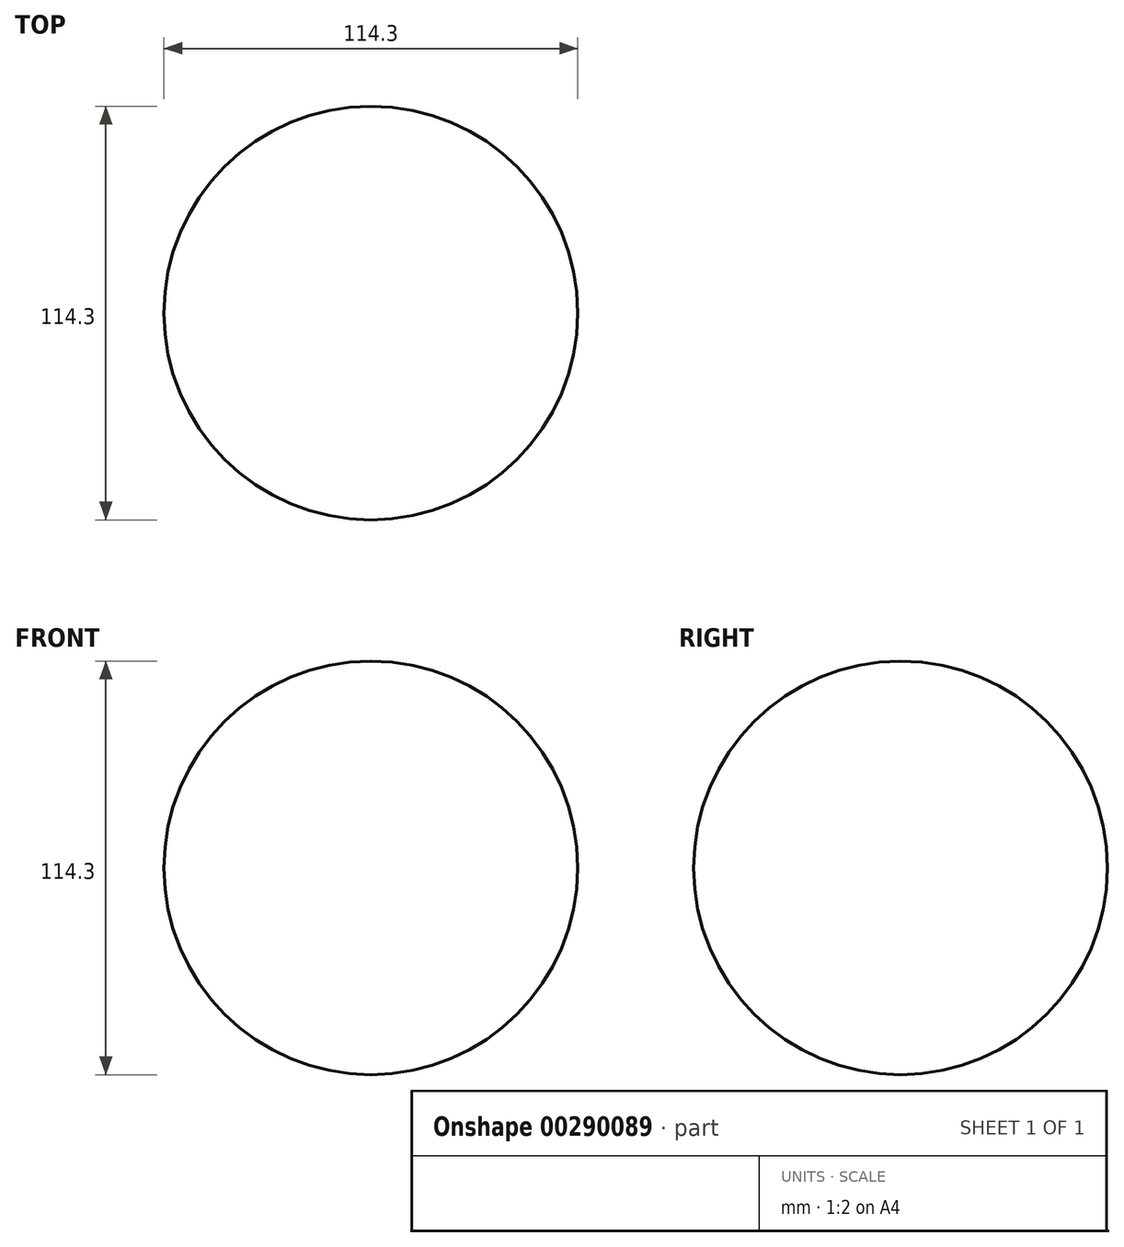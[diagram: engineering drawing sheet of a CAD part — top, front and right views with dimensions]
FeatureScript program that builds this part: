
annotation { "Feature Type Name" : "Feature", "Feature Type Description" : "" }
export const myFeature = defineFeature(function(context is Context, id is Id, definition is map)
    precondition{}
    {
        {
            var Q0;
            Q0=qCreatedBy(makeId("Top.planeOp"),FACE);
            var sketch = newSketch(context, id + "F0", { "sketchPlane" : qUnion([Q0])});
            skArc(sketch, "E0", {"start": v(0, 57.15) * mm, "mid": v(-57.15, 0) * mm, "end": v(0, -57.15) * mm});
            skLineSegment(sketch, "E1", {"start": v(0, 57.15) * mm, "end": v(0, -57.15) * mm});
            skSolve(sketch);
        }
        {
            var Q0;
            Q0=makeQuery(id+"F0.imprint","IMPRINT",FACE,{"disambiguationData":[TD([[makeQuery(id+"F0.imprint","IMPRINT",EDGE,{"derivedFrom":sQuery(id+"F0.wireOp",EDGE,"E0")}),1.0]])]});
            var Q1;
            Q1=sQuery(id+"F0.wireOp",EDGE,"E1");
            var Q2;
            Q2=sQuery(id+"F0.wireOp",EDGE,"E1");
            revolve(context, id + "F1", {"entities" : qUnion([Q0]), "surfaceEntities" : qUnion([Q1]), "axis" : qUnion([Q2]), "revolveType" : RevolveType.FULL});
        }
    });
